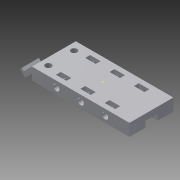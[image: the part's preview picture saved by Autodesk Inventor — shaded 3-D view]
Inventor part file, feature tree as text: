
AUTODESK INVENTOR PART (.ipt)
format: ipt  version: 2015 (Build 190159000, 159)  size: 218,112 bytes
history: native  units: mm
features: sketch x8, other x4, plane x2
ambient origin geometry x8: Origin, YZ Plane, XZ Plane, XY Plane, X Axis, Y Axis, Z Axis, Center Point
bodies: Body1 (feature_tree)
feature tree (14):
  other  "dumper_base_v1_SOCKET.ipt"
  other  "Sólido2::dumper_base_v1_SOCKET.ipt"
  other  "OperaciónIdentificador1"
  sketch  "Boceto1"  dims[d0=10.0mm]
  sketch  "Boceto2"
  sketch  "Boceto4"
  sketch  "Boceto5"
  sketch  "Boceto10"
  sketch  "Boceto11"
  sketch  "Boceto12"
  sketch  "Boceto19"
  plane  "Plano de trabajo1"
  plane  "Plano de trabajo2"
  other  "Sólido1"
